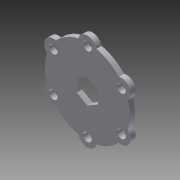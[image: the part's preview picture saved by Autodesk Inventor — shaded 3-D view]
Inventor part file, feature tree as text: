
AUTODESK INVENTOR PART (.ipt)
format: ipt  version: 2014 SP1 (Build 180222100, 222)  size: 142,336 bytes
history: native  units: in
note: dims shown in document units (in); Inventor stores cm internally (conversion verified against a paired STEP export)
features: extrude x3, sketch x2
ambient origin geometry x8: Origin, YZ Plane, XZ Plane, XY Plane, X Axis, Y Axis, Z Axis, Center Point
bodies: Solid1 (feature_tree)
feature tree (5):
  extrude  "Extrusion1"  Depth=0.204in
  sketch  "Sketch3"  dims[d8=0.125in d9=0.0in d10=2.3622in d12=360.0deg d14=0.438in d15=2.022in d16=2.3622in d18=360.0deg d20=0.125in d21=0.0in d22=0.125in d23=0.0in]
  extrude  "Extrusion3"  Depth=0.125in TaperAngle=360.0deg
  extrude  "Extrusion2"  Depth=0.125in
  sketch  "Sketch1"  dims[d6=1.875in d7=0.204in]
